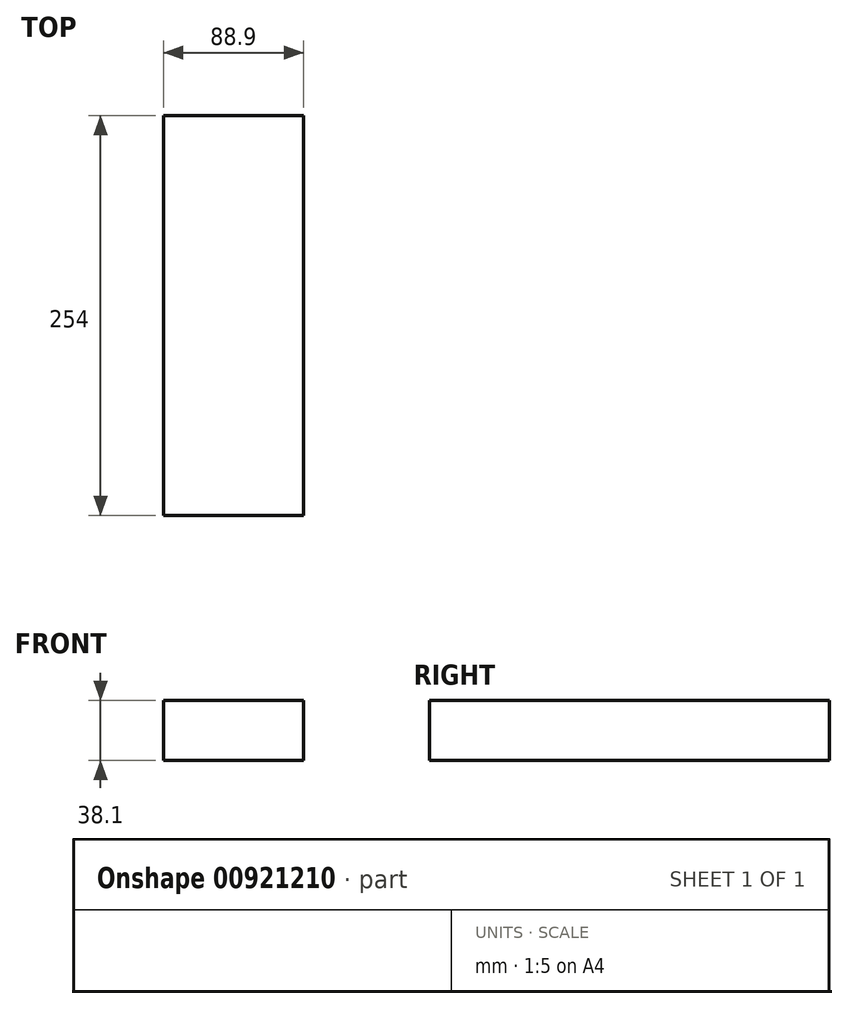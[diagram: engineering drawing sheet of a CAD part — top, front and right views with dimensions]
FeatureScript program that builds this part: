
annotation { "Feature Type Name" : "Feature", "Feature Type Description" : "" }
export const myFeature = defineFeature(function(context is Context, id is Id, definition is map)
    precondition{}
    {
        {
            var Q0;
            Q0=qCreatedBy(makeId("Front.planeOp"),FACE);
            var sketch = newSketch(context, id + "F0", { "sketchPlane" : qUnion([Q0])});
            skLineSegment(sketch, "E0.bottom", {"start": v(-44.45, 19.05) * mm, "end": v(44.45, 19.05) * mm});
            skLineSegment(sketch, "E0.top", {"start": v(-44.45, -19.05) * mm, "end": v(44.45, -19.05) * mm});
            skLineSegment(sketch, "E0.left", {"start": v(-44.45, 19.05) * mm, "end": v(-44.45, -19.05) * mm});
            skLineSegment(sketch, "E0.right", {"start": v(44.45, 19.05) * mm, "end": v(44.45, -19.05) * mm});
            skPoint(sketch, "E0.middle", {"position": v(0, 0) * mm});
            skSolve(sketch);
        }
        {
            var Q0;
            Q0 = qSketchRegion(id + "F0", true);
            extrude(context, id + "F1", {"entities" : qUnion([Q0]), "endBound" : BoundingType.SYMMETRIC, "depth" : 254 * mm, "offsetDistance" : 25.4 * mm});
        }
    });
